# Revit family: Wireless Control Panel _185W
name_source: partatom
category: Electrical Fixtures
revit_build: Autodesk Revit 2018 (Build: 20170223_1515(x64)
units: mm (PartAtom-declared; Revit-internal decimal feet)

## family parameters
Always vertical = Yes
Cut with Voids When Loaded = No
Maintain Annotation Orientation = No
OmniClass Number = 23.80.00.00
OmniClass Title = Electric Power and Lighting
Part Type = Normal
Room Calculation Point = No
Round Connector Dimension = Use Diameter
Shared = No
Work Plane-Based = Yes

## types (1)
- Wireless Control Panel
    Colour = White (RAL 9016)
    Communication technology = Bluetooth® Low Energy (2.4 GHz)
    Default Elevation = 0 mm  [stored 0 ft]
    Dimensions = 81 mm × 81 mm × 14 mm
    Lifetime = Over 50,000 actuations (button presses) according to EN 60669 / VDE 0632
    Manufacturer = Helvar
    Material = Plastic, PC
    Model = 185W
    Mounting = Adhesive double-sided mounting pad (enclosed) or screwing onto flat surface using ⌀ 3 mm countersunk screws (not included
    Wiring = No wiring is required (power or communications

note: [stored X ft] marks values corroborated as IEEE doubles in the binary element streams (Revit-internal decimal feet)

## geometry (parser evidence)
native form markers: Sweep x3
no freeform markers — native parametric forms only
